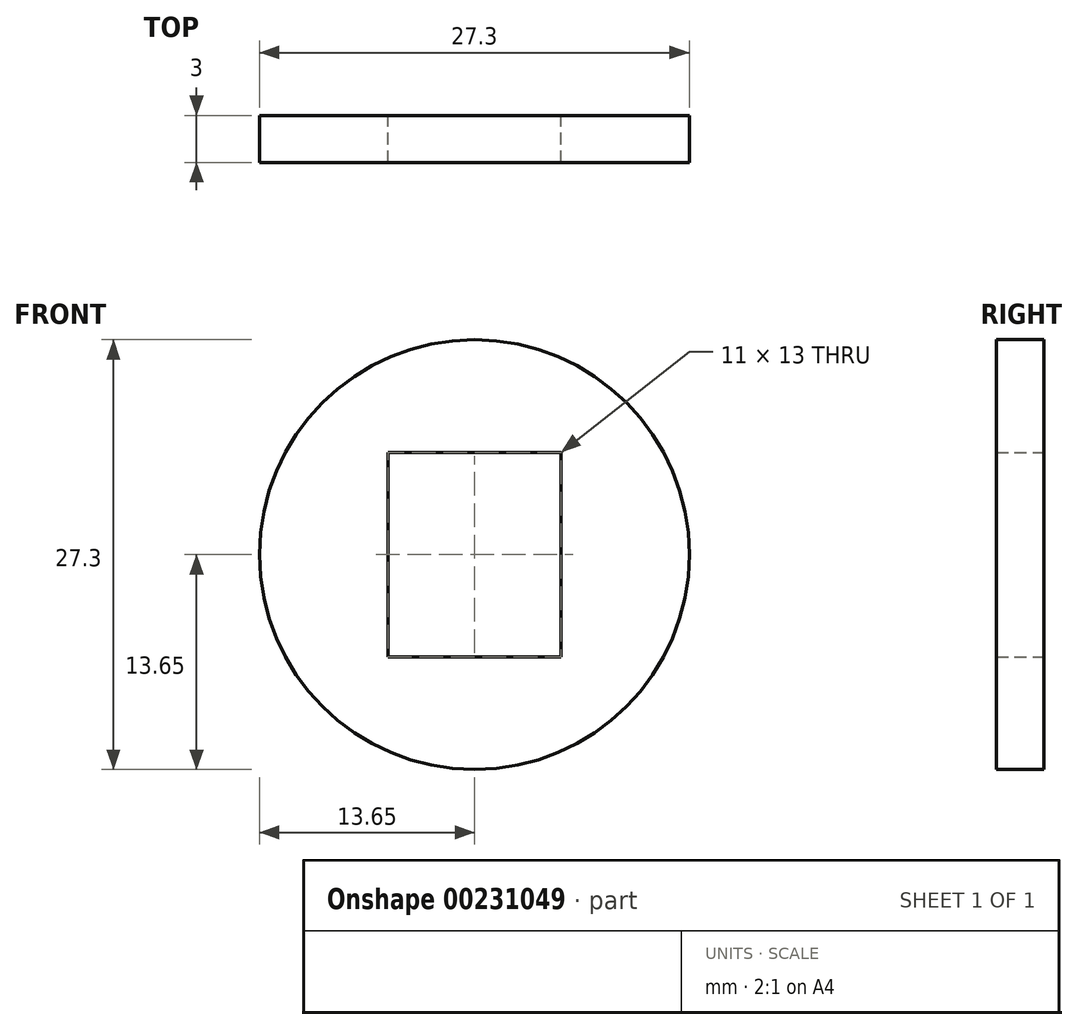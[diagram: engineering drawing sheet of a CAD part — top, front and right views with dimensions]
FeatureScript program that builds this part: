
annotation { "Feature Type Name" : "Feature", "Feature Type Description" : "" }
export const myFeature = defineFeature(function(context is Context, id is Id, definition is map)
    precondition{}
    {
        {
            var Q0;
            Q0=qCreatedBy(makeId("Front.planeOp"),FACE);
            var sketch = newSketch(context, id + "F0", { "sketchPlane" : qUnion([Q0])});
            skLineSegment(sketch, "E0.bottom", {"start": v(5.5, 6.5) * mm, "end": v(-5.5, 6.5) * mm});
            skLineSegment(sketch, "E0.top", {"start": v(5.5, -6.5) * mm, "end": v(-5.5, -6.5) * mm});
            skLineSegment(sketch, "E0.left", {"start": v(5.5, 6.5) * mm, "end": v(5.5, -6.5) * mm});
            skLineSegment(sketch, "E0.right", {"start": v(-5.5, 6.5) * mm, "end": v(-5.5, -6.5) * mm});
            skPoint(sketch, "E0.middle", {"position": v(0, 0) * mm});
            skCircle(sketch, "E1", {"center": v(0, 0) * mm, "radius": 13.65 * mm});
            skSolve(sketch);
        }
        {
            var Q0;
            Q0=makeQuery(id+"F0.imprint","IMPRINT",FACE,{"disambiguationData":[TD([[makeQuery(id+"F0.imprint","IMPRINT",EDGE,{"derivedFrom":sQuery(id+"F0.wireOp",EDGE,"E0.bottom")}),-1.0]])]});
            extrude(context, id + "F1", {"entities" : qUnion([Q0]), "depth" : 3 * mm});
        }
    });
